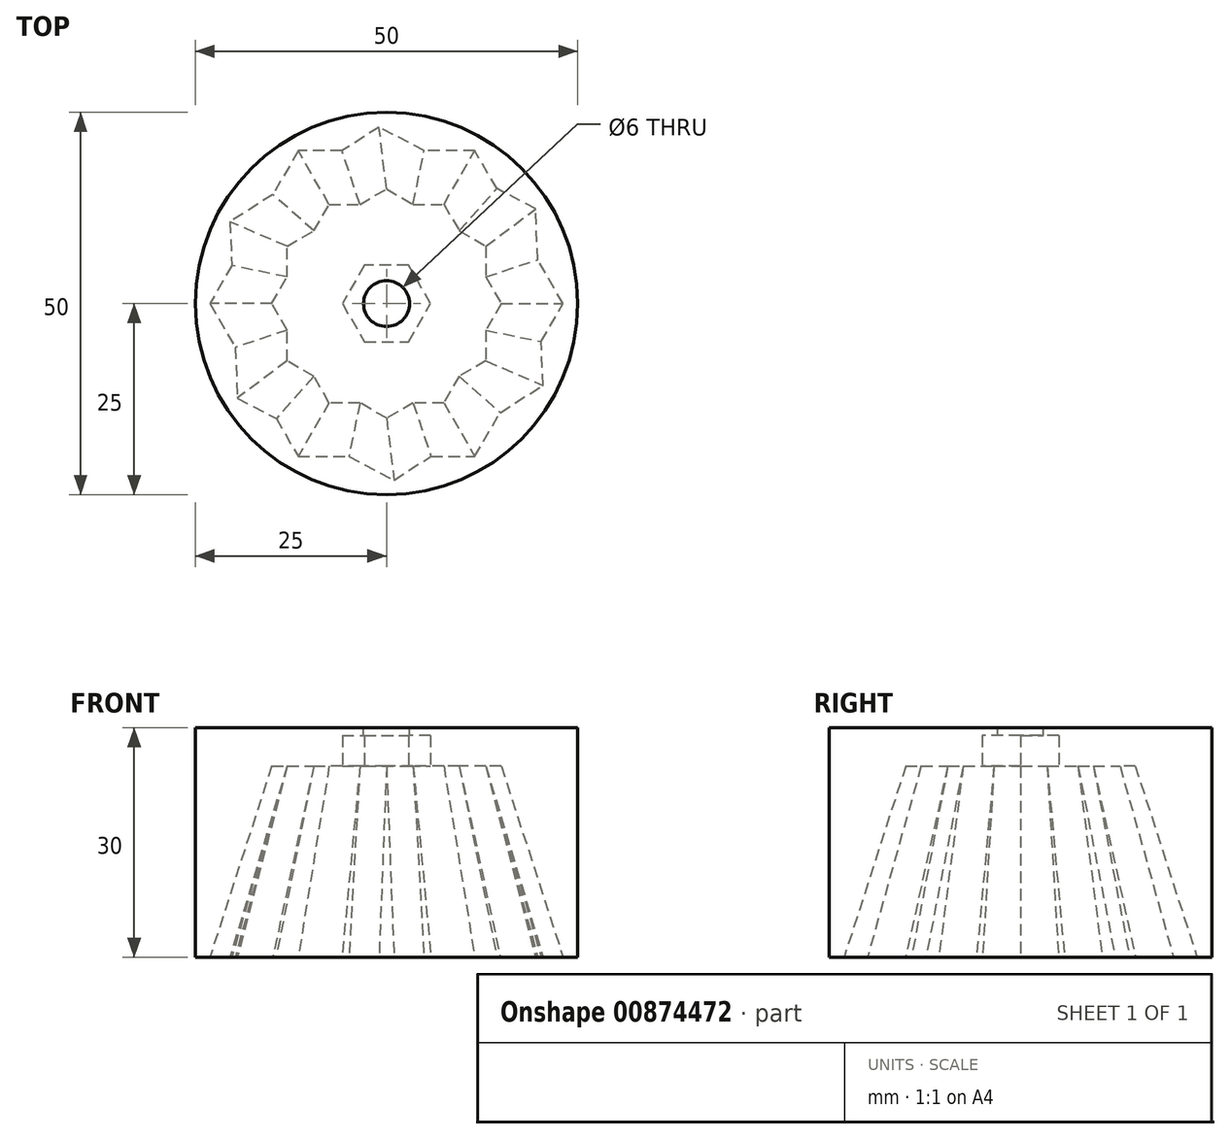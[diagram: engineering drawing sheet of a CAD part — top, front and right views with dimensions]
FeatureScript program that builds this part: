
annotation { "Feature Type Name" : "Feature", "Feature Type Description" : "" }
export const myFeature = defineFeature(function(context is Context, id is Id, definition is map)
    precondition{}
    {
        {
            var Q0;
            Q0=qCreatedBy(makeId("Top.planeOp"),FACE);
            var sketch = newSketch(context, id + "F0", { "sketchPlane" : qUnion([Q0])});
            skCircle(sketch, "E0", {"center": v(0, 0) * mm, "radius": 25 * mm});
            skSolve(sketch);
        }
        {
            var Q0;
            Q0=makeQuery(id+"F0.imprint","IMPRINT",FACE,{"disambiguationData":[TD([[makeQuery(id+"F0.imprint","IMPRINT",EDGE,{"derivedFrom":sQuery(id+"F0.wireOp",EDGE,"E0")}),1.0]])]});
            extrude(context, id + "F1", {"entities" : qUnion([Q0]), "depth" : 25 * mm, "offsetDistance" : 25 * mm});
        }
        {
            var Q0;
            Q0=makeQuery(id+"F1.opExtrude","CAP_FACE",FACE,{"disambiguationData":[OSD([sQuery(id+"F0.wireOp",EDGE,"E0")])],"isStart":true});
            var sketch = newSketch(context, id + "F2", { "sketchPlane" : qUnion([Q0])});
            skLineSegment(sketch, "E1.0", {"start": v(-11.55, 20) * mm, "end": v(-4.91, 20) * mm});
            skLineSegment(sketch, "E1.1", {"start": v(11.55, 20) * mm, "end": v(14.87, 14.25) * mm});
            skLineSegment(sketch, "E1.2", {"start": v(23.1, 0) * mm, "end": v(19.78, -5.75) * mm});
            skLineSegment(sketch, "E1.3", {"start": v(11.55, -20) * mm, "end": v(4.91, -20) * mm});
            skLineSegment(sketch, "E1.4", {"start": v(-11.55, -20) * mm, "end": v(-14.87, -14.25) * mm});
            skLineSegment(sketch, "E1.5", {"start": v(-23.1, 0) * mm, "end": v(-19.78, 5.75) * mm});
            skPoint(sketch, "E1.0.midPoint", {"position": v(0, 20) * mm});
            skLineSegment(sketch, "E2.0", {"start": v(-20.47, -10.7) * mm, "end": v(-20.23, -4.97) * mm});
            skLineSegment(sketch, "E2.1", {"start": v(-19.5, 12.38) * mm, "end": v(-14.41, 15.03) * mm});
            skLineSegment(sketch, "E2.2", {"start": v(0.97, 23.07) * mm, "end": v(5.81, 20) * mm});
            skLineSegment(sketch, "E2.3", {"start": v(20.47, 10.7) * mm, "end": v(20.23, 4.97) * mm});
            skLineSegment(sketch, "E2.4", {"start": v(19.5, -12.38) * mm, "end": v(14.41, -15.03) * mm});
            skLineSegment(sketch, "E2.5", {"start": v(-0.97, -23.07) * mm, "end": v(-5.81, -20) * mm});
            skPoint(sketch, "E2.0.midPoint", {"position": v(-19.98, 0.84) * mm});
            skLineSegment(sketch, "E3.trimOffspring", {"start": v(-4.91, 20) * mm, "end": v(0.97, 23.07) * mm});
            skLineSegment(sketch, "E4.trimOffspring", {"start": v(5.81, 20) * mm, "end": v(11.55, 20) * mm});
            skLineSegment(sketch, "E5.trimOffspring", {"start": v(14.87, 14.25) * mm, "end": v(20.47, 10.7) * mm});
            skLineSegment(sketch, "E6.trimOffspring", {"start": v(20.23, 4.97) * mm, "end": v(23.1, 0) * mm});
            skLineSegment(sketch, "E7.trimOffspring", {"start": v(19.78, -5.75) * mm, "end": v(19.5, -12.38) * mm});
            skLineSegment(sketch, "E8.trimOffspring", {"start": v(14.41, -15.03) * mm, "end": v(11.55, -20) * mm});
            skLineSegment(sketch, "E9.trimOffspring", {"start": v(4.91, -20) * mm, "end": v(-0.97, -23.07) * mm});
            skLineSegment(sketch, "E10.trimOffspring", {"start": v(-5.81, -20) * mm, "end": v(-11.55, -20) * mm});
            skLineSegment(sketch, "E11.trimOffspring", {"start": v(-14.87, -14.25) * mm, "end": v(-20.47, -10.7) * mm});
            skLineSegment(sketch, "E12.trimOffspring", {"start": v(-20.23, -4.97) * mm, "end": v(-23.1, 0) * mm});
            skLineSegment(sketch, "E13.trimOffspring", {"start": v(-19.78, 5.75) * mm, "end": v(-19.5, 12.38) * mm});
            skPoint(sketch, "E1.cCircle.center.orphan", {"position": v(0, 0) * mm});
            skLineSegment(sketch, "E14.trimOffspring", {"start": v(-14.41, 15.03) * mm, "end": v(-11.55, 20) * mm});
            skSolve(sketch);
        }
        {
            var Q0;
            Q0=makeQuery(id+"F1.opExtrude","CAP_FACE",FACE,{"disambiguationData":[OSD([sQuery(id+"F0.wireOp",EDGE,"E0")])],"isStart":false});
            var sketch = newSketch(context, id + "F3", { "sketchPlane" : qUnion([Q0])});
            skLineSegment(sketch, "E15.0", {"start": v(-7.5, 13) * mm, "end": v(-3.48, 13) * mm});
            skLineSegment(sketch, "E15.1", {"start": v(7.5, 13) * mm, "end": v(9.5, 9.5) * mm});
            skLineSegment(sketch, "E15.2", {"start": v(15, 0) * mm, "end": v(13, -3.48) * mm});
            skLineSegment(sketch, "E15.3", {"start": v(7.5, -13) * mm, "end": v(3.48, -13) * mm});
            skLineSegment(sketch, "E15.4", {"start": v(-7.5, -13) * mm, "end": v(-9.5, -9.5) * mm});
            skLineSegment(sketch, "E15.5", {"start": v(-15, 0) * mm, "end": v(-13, 3.48) * mm});
            skPoint(sketch, "E15.0.midPoint", {"position": v(0, 13) * mm});
            skLineSegment(sketch, "E16.0", {"start": v(-13, -7.5) * mm, "end": v(-13, -3.48) * mm});
            skLineSegment(sketch, "E16.1", {"start": v(-13, 7.5) * mm, "end": v(-9.5, 9.5) * mm});
            skLineSegment(sketch, "E16.2", {"start": v(0, 15) * mm, "end": v(3.48, 13) * mm});
            skLineSegment(sketch, "E16.3", {"start": v(13, 7.5) * mm, "end": v(13, 3.48) * mm});
            skLineSegment(sketch, "E16.4", {"start": v(13, -7.5) * mm, "end": v(9.5, -9.5) * mm});
            skLineSegment(sketch, "E16.5", {"start": v(0, -15) * mm, "end": v(-3.48, -13) * mm});
            skPoint(sketch, "E16.0.midPoint", {"position": v(-13, 0) * mm});
            skLineSegment(sketch, "E17.trimOffspring", {"start": v(-3.48, 13) * mm, "end": v(0, 15) * mm});
            skLineSegment(sketch, "E18.trimOffspring", {"start": v(3.48, 13) * mm, "end": v(7.5, 13) * mm});
            skLineSegment(sketch, "E19.trimOffspring", {"start": v(9.5, 9.5) * mm, "end": v(13, 7.5) * mm});
            skLineSegment(sketch, "E20.trimOffspring", {"start": v(13, 3.48) * mm, "end": v(15, 0) * mm});
            skLineSegment(sketch, "E21.trimOffspring", {"start": v(13, -3.48) * mm, "end": v(13, -7.5) * mm});
            skLineSegment(sketch, "E22.trimOffspring", {"start": v(9.5, -9.5) * mm, "end": v(7.5, -13) * mm});
            skLineSegment(sketch, "E23.trimOffspring", {"start": v(3.48, -13) * mm, "end": v(0, -15) * mm});
            skLineSegment(sketch, "E24.trimOffspring", {"start": v(-3.48, -13) * mm, "end": v(-7.5, -13) * mm});
            skLineSegment(sketch, "E25.trimOffspring", {"start": v(-9.5, -9.5) * mm, "end": v(-13, -7.5) * mm});
            skLineSegment(sketch, "E26.trimOffspring", {"start": v(-13, -3.48) * mm, "end": v(-15, 0) * mm});
            skLineSegment(sketch, "E27.trimOffspring", {"start": v(-13, 3.48) * mm, "end": v(-13, 7.5) * mm});
            skPoint(sketch, "E15.cCircle.center.orphan", {"position": v(0, 0) * mm});
            skLineSegment(sketch, "E28.trimOffspring", {"start": v(-9.5, 9.5) * mm, "end": v(-7.5, 13) * mm});
            skSolve(sketch);
        }
        {
            var Q1;
            Q1=makeQuery(id+"F3.imprint","IMPRINT",FACE,{"disambiguationData":[TD([[makeQuery(id+"F3.imprint","IMPRINT",EDGE,{"derivedFrom":sQuery(id+"F3.wireOp",EDGE,"E15.0")}),-1.0]])]});
            var Q2;
            Q2=makeQuery(id+"F2.imprint","IMPRINT",FACE,{"disambiguationData":[TD([[makeQuery(id+"F2.imprint","IMPRINT",EDGE,{"derivedFrom":sQuery(id+"F2.wireOp",EDGE,"E1.0")}),-1.0]])]});
            loft(context, id + "F4", {"operationType" : NewBodyOperationType.REMOVE, "sheetProfilesArray" : [{ "sheetProfileEntities" : qUnion([Q1]) }, { "sheetProfileEntities" : qUnion([Q2]) }]});
        }
        {
            var Q0;
            Q0=makeQuery(id+"F1.opExtrude","CAP_FACE",FACE,{"disambiguationData":[OSD([sQuery(id+"F0.wireOp",EDGE,"E0")])],"isStart":false});
            var sketch = newSketch(context, id + "F5", { "sketchPlane" : qUnion([Q0])});
            skCircle(sketch, "E29", {"center": v(0, 0) * mm, "radius": 25 * mm});
            skSolve(sketch);
        }
        {
            var Q0;
            Q0 = qSketchRegion(id + "F5", true);
            extrude(context, id + "F6", {"entities" : qUnion([Q0]), "operationType" : NewBodyOperationType.ADD, "depth" : 5 * mm, "offsetDistance" : 25 * mm});
        }
        {
            var Q0;
            Q0=makeQuery(id+"F6.opExtrude","CAP_FACE",FACE,{"disambiguationData":[OSD([sQuery(id+"F5.wireOp",EDGE,"E29")])],"isStart":true});
            var sketch = newSketch(context, id + "F7", { "sketchPlane" : qUnion([Q0])});
            skCircle(sketch, "E30.cCircle", {"center": v(0, 0) * mm, "radius": 5 * mm, "construction": true});
            skLineSegment(sketch, "E30.0", {"start": v(-2.89, 5) * mm, "end": v(2.89, 5) * mm});
            skLineSegment(sketch, "E30.1", {"start": v(2.89, 5) * mm, "end": v(5.77, 0) * mm});
            skLineSegment(sketch, "E30.2", {"start": v(5.77, 0) * mm, "end": v(2.89, -5) * mm});
            skLineSegment(sketch, "E30.3", {"start": v(2.89, -5) * mm, "end": v(-2.89, -5) * mm});
            skLineSegment(sketch, "E30.4", {"start": v(-2.89, -5) * mm, "end": v(-5.77, 0) * mm});
            skLineSegment(sketch, "E30.5", {"start": v(-5.77, 0) * mm, "end": v(-2.89, 5) * mm});
            skPoint(sketch, "E30.0.midPoint", {"position": v(0, 5) * mm});
            skSolve(sketch);
        }
        {
            var Q0;
            Q0=makeQuery(id+"F7.imprint","IMPRINT",FACE,{"disambiguationData":[TD([[makeQuery(id+"F7.imprint","IMPRINT",EDGE,{"derivedFrom":sQuery(id+"F7.wireOp",EDGE,"E30.0")}),-1.0]])]});
            extrude(context, id + "F8", {"entities" : qUnion([Q0]), "operationType" : NewBodyOperationType.REMOVE, "oppositeDirection" : true, "depth" : 4 * mm, "offsetDistance" : 25 * mm});
        }
        {
            var Q0;
            Q0=makeQuery(id+"F6.opExtrude","CAP_FACE",FACE,{"disambiguationData":[OSD([sQuery(id+"F5.wireOp",EDGE,"E29")])],"isStart":false});
            var sketch = newSketch(context, id + "F9", { "sketchPlane" : qUnion([Q0])});
            skCircle(sketch, "E31", {"center": v(0, 0) * mm, "radius": 3 * mm});
            skSolve(sketch);
        }
        {
            var Q0;
            Q0=makeQuery(id+"F9.imprint","IMPRINT",FACE,{"disambiguationData":[TD([[makeQuery(id+"F9.imprint","IMPRINT",EDGE,{"derivedFrom":sQuery(id+"F9.wireOp",EDGE,"E31")}),1.0]])]});
            extrude(context, id + "F10", {"entities" : qUnion([Q0]), "operationType" : NewBodyOperationType.REMOVE, "oppositeDirection" : true, "depth" : 25 * mm, "offsetDistance" : 25 * mm});
        }
    });
